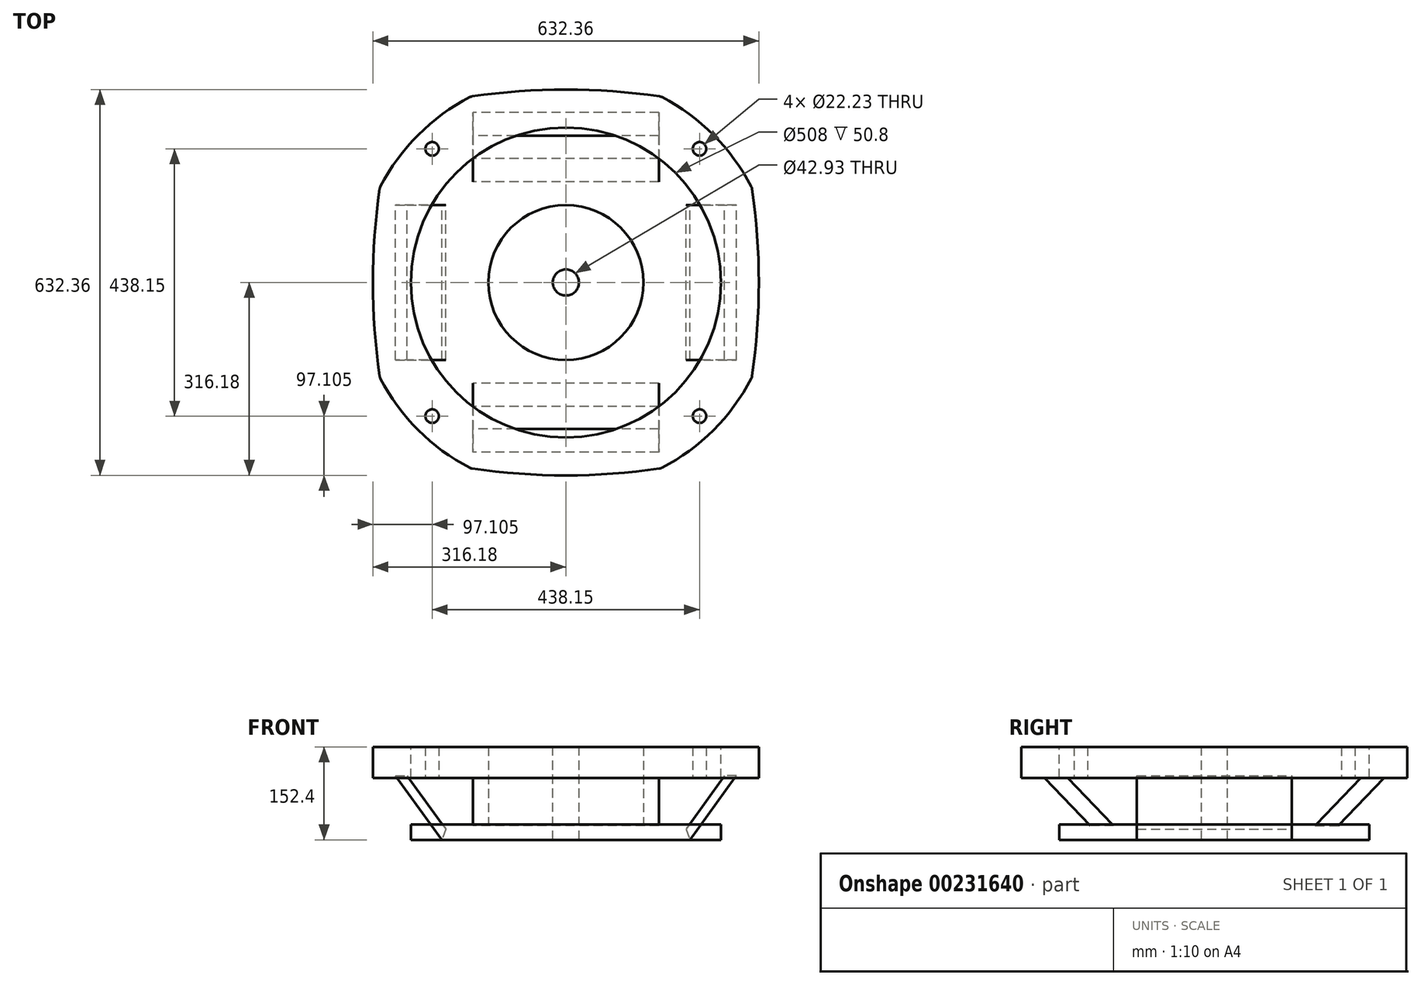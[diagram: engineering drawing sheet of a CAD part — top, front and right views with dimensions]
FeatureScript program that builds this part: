
annotation { "Feature Type Name" : "Feature", "Feature Type Description" : "" }
export const myFeature = defineFeature(function(context is Context, id is Id, definition is map)
    precondition{}
    {
        {
            var Q0;
            Q0=qCreatedBy(makeId("Top.planeOp"),FACE);
            var sketch = newSketch(context, id + "F0", { "sketchPlane" : qUnion([Q0])});
            skCircle(sketch, "E0", {"center": v(0, 0) * mm, "radius": 254 * mm});
            skSolve(sketch);
        }
        {
            var Q0;
            Q0 = qSketchRegion(id + "F0", true);
            extrude(context, id + "F1", {"entities" : qUnion([Q0]), "depth" : 25.4 * mm});
        }
        {
            var Q0;
            Q0=qCreatedBy(makeId("Top.planeOp"),FACE);
            cPlane(context, id + "F2", {"entities" : qUnion([Q0]), "cplaneType" : CPlaneType.OFFSET, "offset" : 152.4 * mm, "width" : 152.4 * mm, "height" : 152.4 * mm});
        }
        {
            var Q0;
            Q0=qCreatedBy(id+"F2.planeOp",FACE);
            var sketch = newSketch(context, id + "F3", { "sketchPlane" : qUnion([Q0])});
            skPoint(sketch, "E1.middle", {"position": v(0, 0) * mm});
            skArc(sketch, "E2", {"start": v(-303.82, -157.33) * mm, "mid": v(-241.93, -241.93) * mm, "end": v(-157.33, -303.82) * mm});
            skPoint(sketch, "E3.orphan", {"position": v(304.8, 304.8) * mm});
            skPoint(sketch, "E4.orphan", {"position": v(304.8, -304.8) * mm});
            skPoint(sketch, "E5.orphan", {"position": v(-304.8, -304.8) * mm});
            skPoint(sketch, "E6.orphan", {"position": v(-304.8, 304.8) * mm});
            skArc(sketch, "E7", {"start": v(153.32, 305.1) * mm, "mid": v(0, 316.18) * mm, "end": v(-153.32, 305.1) * mm});
            skArc(sketch, "E8", {"start": v(-305.1, 153.32) * mm, "mid": v(-316.18, 0) * mm, "end": v(-305.1, -153.32) * mm});
            skArc(sketch, "E9", {"start": v(305.1, -153.32) * mm, "mid": v(316.18, 0) * mm, "end": v(305.1, 153.32) * mm});
            skArc(sketch, "E10", {"start": v(-153.32, -305.1) * mm, "mid": v(0, -316.18) * mm, "end": v(153.32, -305.1) * mm});
            skArc(sketch, "E11.trimOffspring", {"start": v(157.33, -303.82) * mm, "mid": v(241.93, -241.93) * mm, "end": v(303.82, -157.33) * mm});
            skArc(sketch, "E12.trimOffspring", {"start": v(303.82, 157.33) * mm, "mid": v(241.93, 241.93) * mm, "end": v(157.33, 303.82) * mm});
            skArc(sketch, "E13.trimOffspring", {"start": v(-157.33, 303.82) * mm, "mid": v(-241.93, 241.93) * mm, "end": v(-303.82, 157.33) * mm});
            skPoint(sketch, "E14.visualSharp", {"position": v(-304.8, -155.42) * mm});
            skArc(sketch, "E14.filletArc", {"start": v(-305.1, -153.32) * mm, "mid": v(-304.63, -155.38) * mm, "end": v(-303.82, -157.33) * mm});
            skPoint(sketch, "E15.visualSharp", {"position": v(-155.42, -304.8) * mm});
            skArc(sketch, "E15.filletArc", {"start": v(-157.33, -303.82) * mm, "mid": v(-155.38, -304.63) * mm, "end": v(-153.32, -305.1) * mm});
            skPoint(sketch, "E16.visualSharp", {"position": v(155.42, -304.8) * mm});
            skArc(sketch, "E16.filletArc", {"start": v(153.32, -305.1) * mm, "mid": v(155.38, -304.63) * mm, "end": v(157.33, -303.82) * mm});
            skPoint(sketch, "E17.visualSharp", {"position": v(304.8, -155.42) * mm});
            skArc(sketch, "E17.filletArc", {"start": v(303.82, -157.33) * mm, "mid": v(304.63, -155.38) * mm, "end": v(305.1, -153.32) * mm});
            skPoint(sketch, "E18.visualSharp", {"position": v(304.8, 155.42) * mm});
            skArc(sketch, "E18.filletArc", {"start": v(305.1, 153.32) * mm, "mid": v(304.63, 155.38) * mm, "end": v(303.82, 157.33) * mm});
            skPoint(sketch, "E19.visualSharp", {"position": v(155.42, 304.8) * mm});
            skArc(sketch, "E19.filletArc", {"start": v(157.33, 303.82) * mm, "mid": v(155.38, 304.63) * mm, "end": v(153.32, 305.1) * mm});
            skPoint(sketch, "E20.visualSharp", {"position": v(-155.42, 304.8) * mm});
            skArc(sketch, "E20.filletArc", {"start": v(-153.32, 305.1) * mm, "mid": v(-155.38, 304.63) * mm, "end": v(-157.33, 303.82) * mm});
            skPoint(sketch, "E21.visualSharp", {"position": v(-304.8, 155.42) * mm});
            skArc(sketch, "E21.filletArc", {"start": v(-303.82, 157.33) * mm, "mid": v(-304.63, 155.38) * mm, "end": v(-305.1, 153.32) * mm});
            skCircle(sketch, "E22", {"center": v(0, 0) * mm, "radius": 254 * mm});
            skSolve(sketch);
        }
        {
            var Q0;
            Q0 = qSketchRegion(id + "F3", true);
            extrude(context, id + "F4", {"entities" : qUnion([Q0]), "oppositeDirection" : true, "depth" : 50.8 * mm});
        }
        {
            var Q0;
            Q0=qCreatedBy(makeId("Front.planeOp"),FACE);
            var sketch = newSketch(context, id + "F5", { "sketchPlane" : qUnion([Q0])});
            skLineSegment(sketch, "E23", {"start": v(0, 0) * mm, "end": v(-203.2, 0) * mm});
            skLineSegment(sketch, "E24", {"start": v(-203.2, 0) * mm, "end": v(-279.3, 105.3) * mm});
            skLineSegment(sketch, "E25", {"start": v(-279.3, 105.3) * mm, "end": v(-260.15, 105.3) * mm});
            skLineSegment(sketch, "E26", {"start": v(-260.15, 105.3) * mm, "end": v(-196.82, 17.66) * mm});
            skLineSegment(sketch, "E27", {"start": v(-196.82, 17.66) * mm, "end": v(-203.2, 0) * mm});
            skLineSegment(sketch, "E28.MirrorCS", {"start": v(203.2, 0) * mm, "end": v(279.3, 105.3) * mm});
            skLineSegment(sketch, "E29.MirrorCS", {"start": v(279.3, 105.3) * mm, "end": v(260.15, 105.3) * mm});
            skLineSegment(sketch, "E30.MirrorCS", {"start": v(260.15, 105.3) * mm, "end": v(196.82, 17.66) * mm});
            skLineSegment(sketch, "E31.MirrorCS", {"start": v(196.82, 17.66) * mm, "end": v(203.2, 0) * mm});
            skSolve(sketch);
        }
        {
            var Q0;
            Q0 = qSketchRegion(id + "F5", true);
            extrude(context, id + "F6", {"entities" : qUnion([Q0]), "endBound" : BoundingType.SYMMETRIC, "depth" : 254 * mm});
        }
        {
            var Q0;
            Q0=qCreatedBy(makeId("Right.planeOp"),FACE);
            var sketch = newSketch(context, id + "F7", { "sketchPlane" : qUnion([Q0])});
            skLineSegment(sketch, "E32", {"start": v(203.2, 23.37) * mm, "end": v(278.46, 101.98) * mm});
            skLineSegment(sketch, "E33", {"start": v(278.46, 101.98) * mm, "end": v(240.36, 101.98) * mm});
            skLineSegment(sketch, "E34", {"start": v(240.36, 101.98) * mm, "end": v(165.1, 23.37) * mm});
            skLineSegment(sketch, "E35", {"start": v(165.1, 23.37) * mm, "end": v(203.2, 23.37) * mm});
            skLineSegment(sketch, "E36.MirrorCS", {"start": v(-203.2, 23.37) * mm, "end": v(-278.46, 101.98) * mm});
            skLineSegment(sketch, "E37.MirrorCS", {"start": v(-278.46, 101.98) * mm, "end": v(-240.36, 101.98) * mm});
            skLineSegment(sketch, "E38.MirrorCS", {"start": v(-240.36, 101.98) * mm, "end": v(-165.1, 23.37) * mm});
            skLineSegment(sketch, "E39", {"start": v(203.2, 23.37) * mm, "end": v(165.1, 23.37) * mm});
            skLineSegment(sketch, "E40", {"start": v(-165.1, 23.37) * mm, "end": v(-203.2, 23.37) * mm});
            skSolve(sketch);
        }
        {
            var Q0;
            Q0 = qSketchRegion(id + "F7", true);
            extrude(context, id + "F8", {"entities" : qUnion([Q0]), "endBound" : BoundingType.SYMMETRIC, "depth" : 304.8 * mm});
        }
        {
            var Q0;
            Q0=makeQuery(id+"F1.opExtrude","CAP_FACE",FACE,{"disambiguationData":[OSD([sQuery(id+"F0.wireOp",EDGE,"E0")])],"isStart":false});
            var sketch = newSketch(context, id + "F9", { "sketchPlane" : qUnion([Q0])});
            skCircle(sketch, "E41", {"center": v(0, 0) * mm, "radius": 127 * mm});
            skSolve(sketch);
        }
        {
            var Q0;
            Q0 = qSketchRegion(id + "F9", true);
            extrude(context, id + "F10", {"entities" : qUnion([Q0]), "operationType" : NewBodyOperationType.ADD, "depth" : 127 * mm});
        }
        {
            var Q0;
            Q0=makeQuery(id+"F10.opExtrude","CAP_FACE",FACE,{"disambiguationData":[OSD([sQuery(id+"F9.wireOp",EDGE,"E41")])],"isStart":false});
            var sketch = newSketch(context, id + "F11", { "sketchPlane" : qUnion([Q0])});
            skCircle(sketch, "E42", {"center": v(0, 0) * mm, "radius": 21.46 * mm});
            skSolve(sketch);
        }
        {
            var Q0;
            Q0 = qSketchRegion(id + "F11", true);
            extrude(context, id + "F12", {"entities" : qUnion([Q0]), "operationType" : NewBodyOperationType.REMOVE, "endBound" : BoundingType.THROUGH_ALL, "oppositeDirection" : true, "depth" : 25.4 * mm});
        }
        {
            var Q0;
            Q0=makeQuery(id+"F4.opExtrude","CAP_FACE",FACE,{"disambiguationData":[OSD([sQuery(id+"F3.wireOp",EDGE,"E2"),sQuery(id+"F3.wireOp",EDGE,"E7"),sQuery(id+"F3.wireOp",EDGE,"E8"),sQuery(id+"F3.wireOp",EDGE,"E9"),sQuery(id+"F3.wireOp",EDGE,"E10"),sQuery(id+"F3.wireOp",EDGE,"E11.trimOffspring"),sQuery(id+"F3.wireOp",EDGE,"E12.trimOffspring"),sQuery(id+"F3.wireOp",EDGE,"E13.trimOffspring"),sQuery(id+"F3.wireOp",EDGE,"E14.filletArc"),sQuery(id+"F3.wireOp",EDGE,"E15.filletArc"),sQuery(id+"F3.wireOp",EDGE,"E16.filletArc"),sQuery(id+"F3.wireOp",EDGE,"E17.filletArc"),sQuery(id+"F3.wireOp",EDGE,"E18.filletArc"),sQuery(id+"F3.wireOp",EDGE,"E19.filletArc"),sQuery(id+"F3.wireOp",EDGE,"E20.filletArc"),sQuery(id+"F3.wireOp",EDGE,"E21.filletArc"),sQuery(id+"F3.wireOp",EDGE,"E22")])],"isStart":false});
            var sketch = newSketch(context, id + "F13", { "sketchPlane" : qUnion([Q0])});
            skPoint(sketch, "E43.middle", {"position": v(0, 0) * mm});
            skCircle(sketch, "E44", {"center": v(219.08, 219.08) * mm, "radius": 11.11 * mm});
            skCircle(sketch, "E45", {"center": v(219.08, -219.08) * mm, "radius": 11.11 * mm});
            skCircle(sketch, "E46", {"center": v(-219.08, -219.08) * mm, "radius": 11.11 * mm});
            skCircle(sketch, "E47", {"center": v(-219.08, 219.08) * mm, "radius": 11.11 * mm});
            skSolve(sketch);
        }
        {
            var Q0;
            Q0 = qSketchRegion(id + "F13", true);
            extrude(context, id + "F14", {"entities" : qUnion([Q0]), "operationType" : NewBodyOperationType.REMOVE, "endBound" : BoundingType.THROUGH_ALL, "oppositeDirection" : true, "depth" : 25.4 * mm});
        }
    });
